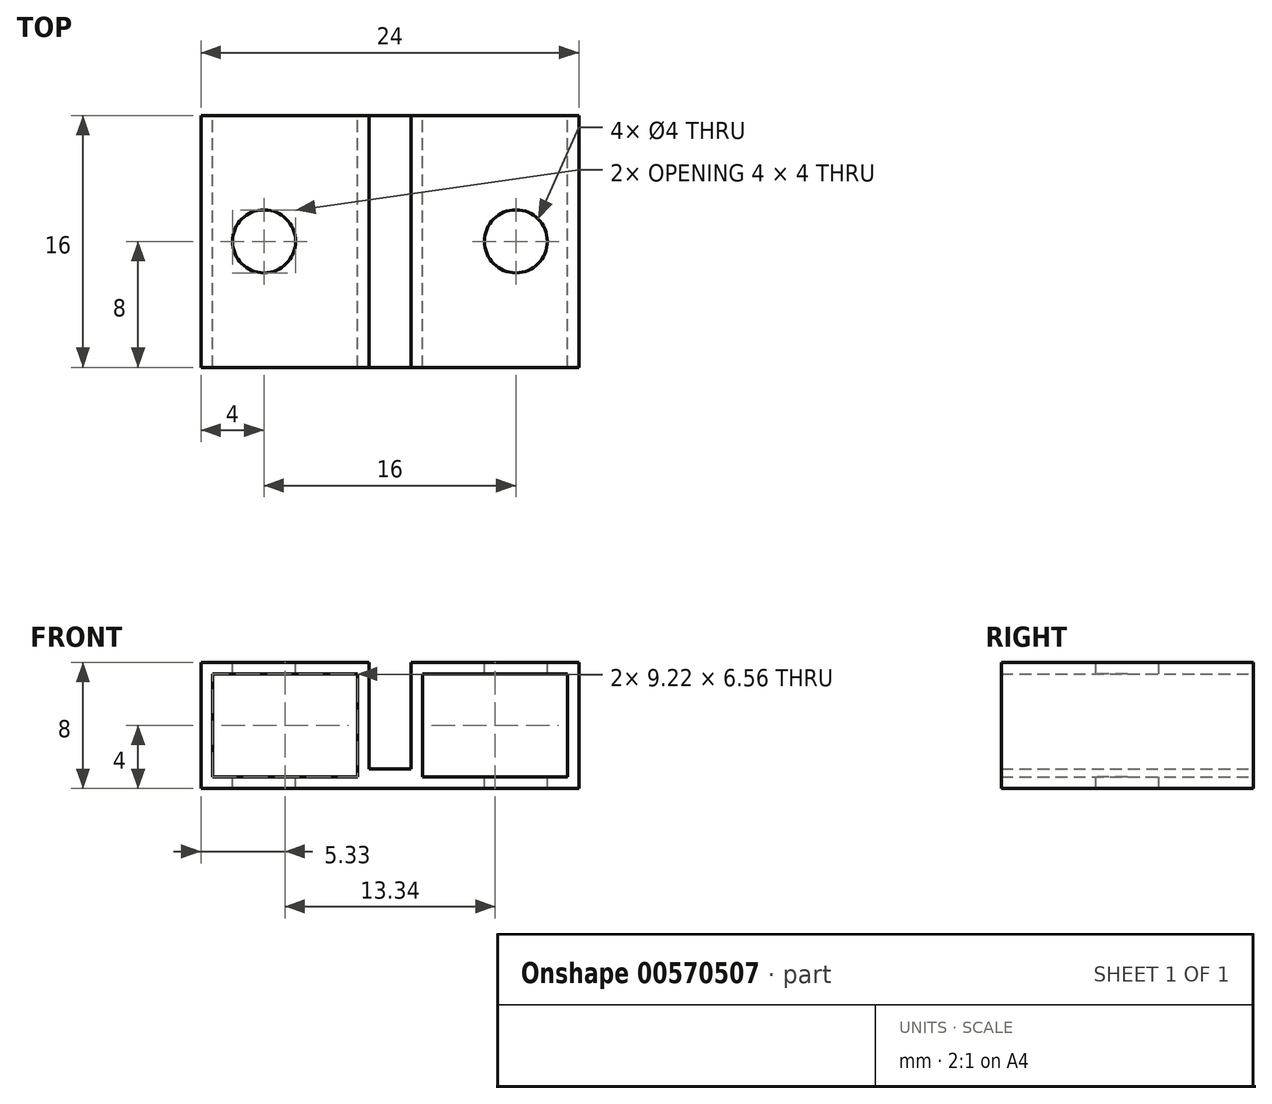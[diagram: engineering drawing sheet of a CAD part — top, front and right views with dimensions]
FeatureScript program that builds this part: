
annotation { "Feature Type Name" : "Feature", "Feature Type Description" : "" }
export const myFeature = defineFeature(function(context is Context, id is Id, definition is map)
    precondition{}
    {
        {
            var Q0;
            Q0=qCreatedBy(makeId("Front.planeOp"),FACE);
            var sketch = newSketch(context, id + "F0", { "sketchPlane" : qUnion([Q0])});
            skLineSegment(sketch, "E0.bottom", {"start": v(-12, 4) * mm, "end": v(12, 4) * mm});
            skLineSegment(sketch, "E0.top", {"start": v(-12, -4) * mm, "end": v(12, -4) * mm});
            skLineSegment(sketch, "E0.left", {"start": v(-12, 4) * mm, "end": v(-12, -4) * mm});
            skLineSegment(sketch, "E0.right", {"start": v(12, 4) * mm, "end": v(12, -4) * mm});
            skPoint(sketch, "E0.middle", {"position": v(0, 0) * mm});
            skLineSegment(sketch, "E1.bottom", {"start": v(-1.34, 10.75) * mm, "end": v(1.34, 10.75) * mm});
            skLineSegment(sketch, "E1.top", {"start": v(-1.34, -2.75) * mm, "end": v(1.34, -2.75) * mm});
            skLineSegment(sketch, "E1.left", {"start": v(-1.34, 10.75) * mm, "end": v(-1.34, -2.75) * mm});
            skLineSegment(sketch, "E1.right", {"start": v(1.34, 10.75) * mm, "end": v(1.34, -2.75) * mm});
            skPoint(sketch, "E1.middle", {"position": v(0, 4) * mm});
            skLineSegment(sketch, "E2.bottom", {"start": v(11.28, -3.28) * mm, "end": v(2.06, -3.28) * mm});
            skLineSegment(sketch, "E2.top", {"start": v(11.28, 3.28) * mm, "end": v(2.06, 3.28) * mm});
            skLineSegment(sketch, "E2.left", {"start": v(11.28, -3.28) * mm, "end": v(11.28, 3.28) * mm});
            skLineSegment(sketch, "E2.right", {"start": v(2.06, -3.28) * mm, "end": v(2.06, 3.28) * mm});
            skLineSegment(sketch, "E3.bottom", {"start": v(-2.06, 3.28) * mm, "end": v(-11.28, 3.28) * mm});
            skLineSegment(sketch, "E3.top", {"start": v(-2.06, -3.28) * mm, "end": v(-11.28, -3.28) * mm});
            skLineSegment(sketch, "E3.left", {"start": v(-2.06, 3.28) * mm, "end": v(-2.06, -3.28) * mm});
            skLineSegment(sketch, "E3.right", {"start": v(-11.28, 3.28) * mm, "end": v(-11.28, -3.28) * mm});
            skLineSegment(sketch, "E4.bottom", {"start": v(-9.78, 3.28) * mm, "end": v(-6.31, 3.28) * mm});
            skLineSegment(sketch, "E4.top", {"start": v(-9.78, -3.28) * mm, "end": v(-6.31, -3.28) * mm});
            skLineSegment(sketch, "E4.left", {"start": v(-9.78, 3.28) * mm, "end": v(-9.78, -3.28) * mm});
            skLineSegment(sketch, "E4.right", {"start": v(-6.31, 3.28) * mm, "end": v(-6.31, -3.28) * mm});
            skLineSegment(sketch, "E5.bottom", {"start": v(6.31, 3.28) * mm, "end": v(9.78, 3.28) * mm});
            skLineSegment(sketch, "E5.top", {"start": v(6.31, -3.28) * mm, "end": v(9.78, -3.28) * mm});
            skLineSegment(sketch, "E5.left", {"start": v(6.31, 3.28) * mm, "end": v(6.31, -3.28) * mm});
            skLineSegment(sketch, "E5.right", {"start": v(9.78, 3.28) * mm, "end": v(9.78, -3.28) * mm});
            skCircle(sketch, "E6", {"center": v(-8, 0) * mm, "radius": 2.16 * mm});
            skCircle(sketch, "E7", {"center": v(8, 0) * mm, "radius": 2.16 * mm});
            skSolve(sketch);
        }
        {
            var Q0;
            Q0=makeQuery(id+"F0.imprint","IMPRINT",FACE,{"disambiguationData":[TD([[makeQuery(id+"F0.imprint","IMPRINT",EDGE,{"derivedFrom":sQuery(id+"F0.wireOp",EDGE,"E0.top")}),1.0]])]});
            var Q1;
            {var subQ0=sQuery(id+"F0.wireOp",EDGE,"E4.bottom");Q1=makeQuery(id+"F0.imprint","IMPRINT",FACE,{"disambiguationData":[TD([[makeQuery(id+"F0.imprint","IMPRINT",EDGE,{"derivedFrom":subQ0}),-1.0]])]});}
            var Q2;
            {var subQ0=sQuery(id+"F0.wireOp",EDGE,"E4.top");Q2=makeQuery(id+"F0.imprint","IMPRINT",FACE,{"disambiguationData":[TD([[makeQuery(id+"F0.imprint","IMPRINT",EDGE,{"derivedFrom":subQ0}),1.0]])]});}
            var Q3;
            {var subQ0=sQuery(id+"F0.wireOp",EDGE,"E5.bottom");Q3=makeQuery(id+"F0.imprint","IMPRINT",FACE,{"disambiguationData":[TD([[makeQuery(id+"F0.imprint","IMPRINT",EDGE,{"derivedFrom":subQ0}),-1.0]])]});}
            var Q4;
            {var subQ0=sQuery(id+"F0.wireOp",EDGE,"E5.top");Q4=makeQuery(id+"F0.imprint","IMPRINT",FACE,{"disambiguationData":[TD([[makeQuery(id+"F0.imprint","IMPRINT",EDGE,{"derivedFrom":subQ0}),1.0]])]});}
            extrude(context, id + "F1", {"entities" : qUnion([Q0, Q1, Q2, Q3, Q4]), "depth" : 16 * mm, "offsetDistance" : 25 * mm});
        }
        {
            var Q0;
            {var subQ0=sQuery(id+"F0.wireOp",EDGE,"E0.bottom");Q0=makeQuery(id+"F1.opExtrude","SWEPT_FACE",FACE,{"disambiguationData":[OSD([subQ0]),TDD([makeQuery(id+"F0.imprint","IMPRINT",EDGE,{"disambiguationData":[TD([[makeQuery(id+"F0.imprint","INTERSECT",VERTEX,{"derivedFrom":[subQ0,sQuery(id+"F0.wireOp",EDGE,"E0.right")]}),1.0]])],"derivedFrom":subQ0})])]});}
            var sketch = newSketch(context, id + "F2", { "sketchPlane" : qUnion([Q0])});
            skCircle(sketch, "E8", {"center": v(8, -8) * mm, "radius": 2 * mm});
            skPoint(sketch, "E8.centerSnap0", {"position": v(12, -8) * mm});
            skCircle(sketch, "E9", {"center": v(-8, -8) * mm, "radius": 2 * mm});
            skSolve(sketch);
        }
        {
            var Q0;
            Q0=makeQuery(id+"F2.imprint","IMPRINT",FACE,{"disambiguationData":[TD([[makeQuery(id+"F2.imprint","IMPRINT",EDGE,{"derivedFrom":sQuery(id+"F2.wireOp",EDGE,"E9")}),1.0]])]});
            var Q1;
            Q1=makeQuery(id+"F2.imprint","IMPRINT",FACE,{"disambiguationData":[TD([[makeQuery(id+"F2.imprint","IMPRINT",EDGE,{"derivedFrom":sQuery(id+"F2.wireOp",EDGE,"E8")}),1.0]])]});
            extrude(context, id + "F3", {"entities" : qUnion([Q0, Q1]), "operationType" : NewBodyOperationType.REMOVE, "oppositeDirection" : true, "depth" : 8.1 * mm, "offsetDistance" : 25 * mm});
        }
    });
